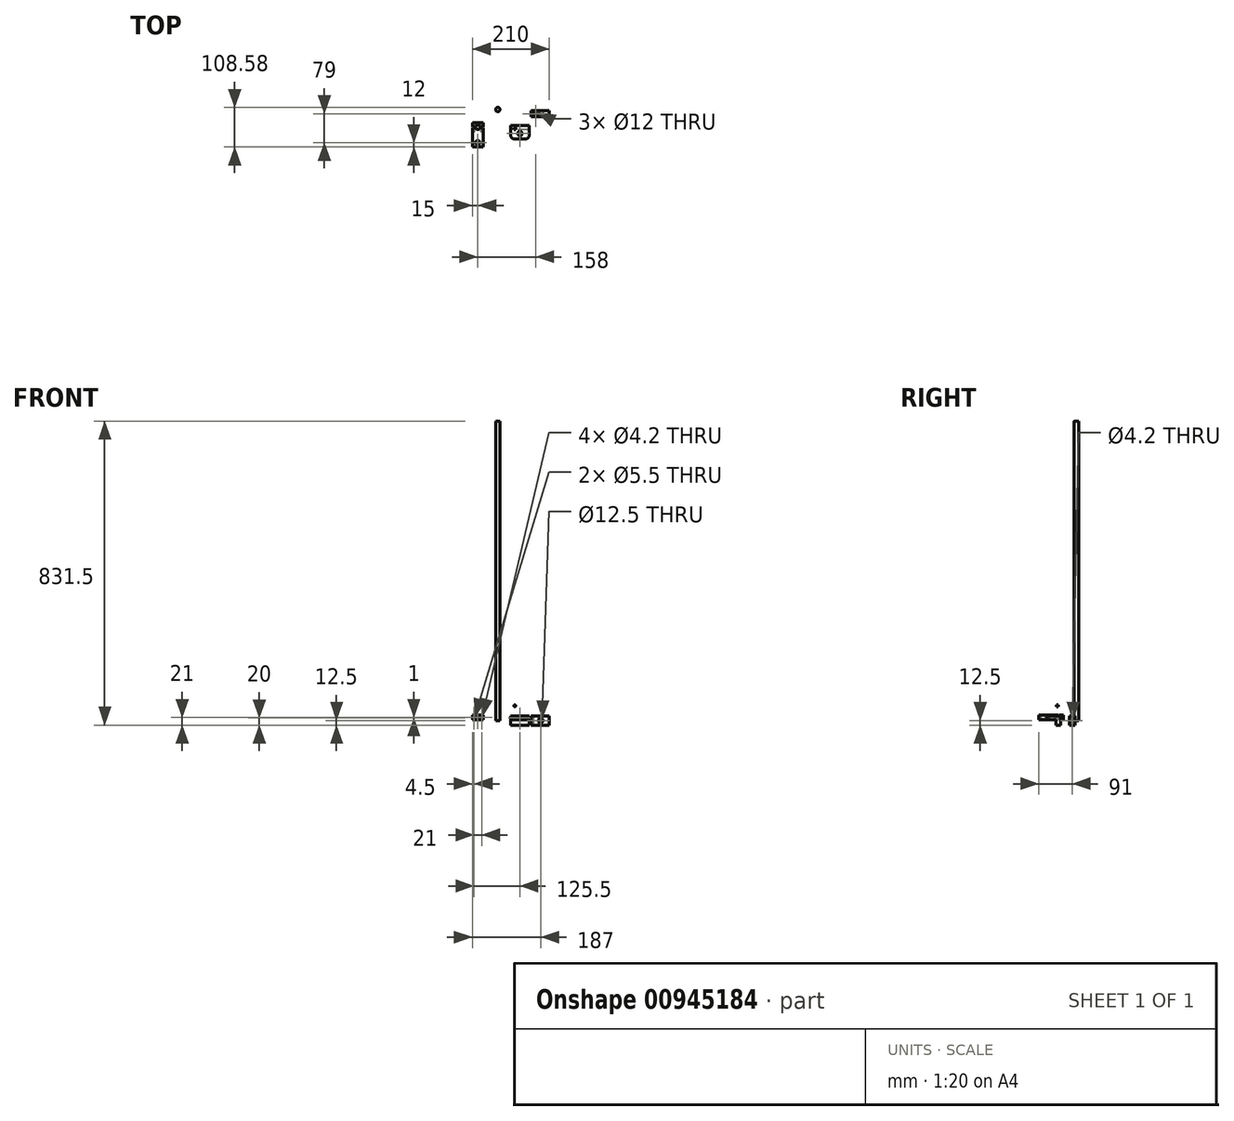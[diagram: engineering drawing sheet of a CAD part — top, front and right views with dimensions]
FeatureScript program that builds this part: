
annotation { "Feature Type Name" : "Feature", "Feature Type Description" : "" }
export const myFeature = defineFeature(function(context is Context, id is Id, definition is map)
    precondition{}
    {
        {
            var Q0;
            Q0=qCreatedBy(makeId("Front.planeOp"),FACE);
            var sketch = newSketch(context, id + "F0", { "sketchPlane" : qUnion([Q0])});
            skLineSegment(sketch, "E0.bottom", {"start": v(25, 12.5) * mm, "end": v(-25, 12.5) * mm});
            skLineSegment(sketch, "E0.top", {"start": v(25, -12.5) * mm, "end": v(-25, -12.5) * mm});
            skLineSegment(sketch, "E0.left", {"start": v(25, 12.5) * mm, "end": v(25, -12.5) * mm});
            skLineSegment(sketch, "E0.right", {"start": v(-25, 12.5) * mm, "end": v(-25, -12.5) * mm});
            skPoint(sketch, "E0.middle", {"position": v(0, 0) * mm});
            skSolve(sketch);
        }
        {
            var Q0;
            Q0 = qSketchRegion(id + "F0", true);
            extrude(context, id + "F1", {"entities" : qUnion([Q0]), "endBound" : BoundingType.SYMMETRIC, "depth" : 12 * mm, "offsetDistance" : 25 * mm});
        }
        {
            var Q0;
            Q0=makeQuery(id+"F1.opExtrude","CAP_FACE",FACE,{"disambiguationData":[OSD([sQuery(id+"F0.wireOp",EDGE,"E0.bottom"),sQuery(id+"F0.wireOp",EDGE,"E0.top"),sQuery(id+"F0.wireOp",EDGE,"E0.left"),sQuery(id+"F0.wireOp",EDGE,"E0.right")])],"isStart":false});
            var sketch = newSketch(context, id + "F2", { "sketchPlane" : qUnion([Q0])});
            skLineSegment(sketch, "E1.bottom", {"start": v(-25, 12.5) * mm, "end": v(25, 12.5) * mm});
            skLineSegment(sketch, "E1.top", {"start": v(-25, 2.5) * mm, "end": v(25, 2.5) * mm});
            skLineSegment(sketch, "E1.left", {"start": v(-25, 12.5) * mm, "end": v(-25, 2.5) * mm});
            skLineSegment(sketch, "E1.right", {"start": v(25, 12.5) * mm, "end": v(25, 2.5) * mm});
            skSolve(sketch);
        }
        {
            var Q0;
            Q0 = qSketchRegion(id + "F2", true);
            extrude(context, id + "F3", {"entities" : qUnion([Q0]), "operationType" : NewBodyOperationType.ADD, "depth" : 25 * mm, "offsetDistance" : 25 * mm});
        }
        {
            var Q0;
            Q0=makeQuery(id+"F3.boolean.opBoolean","MERGE",FACE,{"derivedFrom":[makeQuery(id+"F1.opExtrude","SWEPT_FACE",FACE,{"disambiguationData":[OSD([sQuery(id+"F0.wireOp",EDGE,"E0.bottom")])]}),makeQuery(id+"F3.opExtrude","SWEPT_FACE",FACE,{"disambiguationData":[OSD([sQuery(id+"F2.wireOp",EDGE,"E1.bottom")])]})]});
            var sketch = newSketch(context, id + "F4", { "sketchPlane" : qUnion([Q0])});
            skCircle(sketch, "E2", {"center": v(0, -16) * mm, "radius": 6 * mm});
            skSolve(sketch);
        }
        {
            var Q0;
            Q0 = qSketchRegion(id + "F4", true);
            extrude(context, id + "F5", {"entities" : qUnion([Q0]), "operationType" : NewBodyOperationType.REMOVE, "endBound" : BoundingType.THROUGH_ALL, "oppositeDirection" : true, "depth" : 25 * mm, "offsetDistance" : 25 * mm});
        }
        {
            var Q0;
            Q0=makeQuery(id+"F3.opExtrude","CAP_EDGE",EDGE,{"disambiguationData":[OSD([sQuery(id+"F2.wireOp",EDGE,"E1.left")])],"isStart":false});
            var Q1;
            Q1=makeQuery(id+"F3.opExtrude","CAP_EDGE",EDGE,{"disambiguationData":[OSD([sQuery(id+"F2.wireOp",EDGE,"E1.right")])],"isStart":false});
            fillet(context, id + "F6", {"entities" : qUnion([Q0, Q1]), "radius" : 10 * mm, "tangentPropagation" : true, "allowEdgeOverflow" : false});
        }
        {
            var Q0;
            Q0=qCreatedBy(makeId("Front.planeOp"),FACE);
            var sketch = newSketch(context, id + "F7", { "sketchPlane" : qUnion([Q0])});
            skLineSegment(sketch, "E3.bottom", {"start": v(-130, 14.5) * mm, "end": v(-100, 14.5) * mm});
            skLineSegment(sketch, "E3.top", {"start": v(-130, 2.5) * mm, "end": v(-100, 2.5) * mm});
            skLineSegment(sketch, "E3.left", {"start": v(-130, 14.5) * mm, "end": v(-130, 2.5) * mm});
            skLineSegment(sketch, "E3.right", {"start": v(-100, 14.5) * mm, "end": v(-100, 2.5) * mm});
            skSolve(sketch);
        }
        {
            var Q0;
            Q0 = qSketchRegion(id + "F7", true);
            extrude(context, id + "F8", {"entities" : qUnion([Q0]), "depth" : 53 * mm, "offsetDistance" : 25 * mm});
        }
        {
            var Q0;
            Q0=makeQuery(id+"F8.opExtrude","SWEPT_FACE",FACE,{"disambiguationData":[OSD([sQuery(id+"F7.wireOp",EDGE,"E3.bottom")])]});
            var sketch = newSketch(context, id + "F9", { "sketchPlane" : qUnion([Q0])});
            skCircle(sketch, "E4", {"center": v(-115, 1) * mm, "radius": 6 * mm});
            skSolve(sketch);
        }
        {
            var Q0;
            Q0 = qSketchRegion(id + "F9", true);
            extrude(context, id + "F10", {"entities" : qUnion([Q0]), "operationType" : NewBodyOperationType.REMOVE, "oppositeDirection" : true, "depth" : 25 * mm, "offsetDistance" : 25 * mm});
        }
        {
            var Q0;
            Q0=makeQuery(id+"F8.opExtrude","SWEPT_FACE",FACE,{"disambiguationData":[OSD([sQuery(id+"F7.wireOp",EDGE,"E3.bottom")])]});
            var sketch = newSketch(context, id + "F11", { "sketchPlane" : qUnion([Q0])});
            skLineSegment(sketch, "E5.bottom", {"start": v(-130, 2) * mm, "end": v(-100, 2) * mm});
            skLineSegment(sketch, "E5.top", {"start": v(-130, 14) * mm, "end": v(-100, 14) * mm});
            skLineSegment(sketch, "E5.left", {"start": v(-130, 2) * mm, "end": v(-130, 14) * mm});
            skLineSegment(sketch, "E5.right", {"start": v(-100, 2) * mm, "end": v(-100, 14) * mm});
            skSolve(sketch);
        }
        {
            var Q0;
            Q0 = qSketchRegion(id + "F11", true);
            extrude(context, id + "F12", {"entities" : qUnion([Q0]), "oppositeDirection" : true, "depth" : 12 * mm, "offsetDistance" : 25 * mm});
        }
        {
            var Q0;
            Q0=makeQuery(id+"F12.opExtrude","CAP_FACE",FACE,{"disambiguationData":[OSD([sQuery(id+"F11.wireOp",EDGE,"E5.bottom"),sQuery(id+"F11.wireOp",EDGE,"E5.top"),sQuery(id+"F11.wireOp",EDGE,"E5.left"),sQuery(id+"F11.wireOp",EDGE,"E5.right")])],"isStart":true});
            var sketch = newSketch(context, id + "F13", { "sketchPlane" : qUnion([Q0])});
            skCircle(sketch, "E6", {"center": v(-115, 1) * mm, "radius": 6 * mm});
            skPoint(sketch, "E6.centerSnap0", {"position": v(-115, 2) * mm});
            skSolve(sketch);
        }
        {
            var Q0;
            Q0 = qSketchRegion(id + "F13", true);
            extrude(context, id + "F14", {"entities" : qUnion([Q0]), "operationType" : NewBodyOperationType.REMOVE, "endBound" : BoundingType.THROUGH_ALL, "oppositeDirection" : true, "depth" : 25 * mm, "offsetDistance" : 25 * mm});
        }
        {
            var Q0;
            Q0=makeQuery(id+"F8.opExtrude","SWEPT_FACE",FACE,{"disambiguationData":[OSD([sQuery(id+"F7.wireOp",EDGE,"E3.bottom")])]});
            var sketch = newSketch(context, id + "F15", { "sketchPlane" : qUnion([Q0])});
            skCircle(sketch, "E7", {"center": v(-115, -41) * mm, "radius": 6 * mm});
            skSolve(sketch);
        }
        {
            var Q0;
            Q0 = qSketchRegion(id + "F15", true);
            extrude(context, id + "F16", {"entities" : qUnion([Q0]), "operationType" : NewBodyOperationType.REMOVE, "endBound" : BoundingType.THROUGH_ALL, "oppositeDirection" : true, "depth" : 25 * mm, "offsetDistance" : 25 * mm});
        }
        {
            var Q0;
            Q0=qCreatedBy(makeId("Top.planeOp"),FACE);
            var sketch = newSketch(context, id + "F17", { "sketchPlane" : qUnion([Q0])});
            skCircle(sketch, "E8", {"center": v(-60.48, 49.58) * mm, "radius": 6 * mm});
            skSolve(sketch);
        }
        {
            var Q0;
            Q0 = qSketchRegion(id + "F17", true);
            extrude(context, id + "F18", {"entities" : qUnion([Q0]), "depth" : 819 * mm, "offsetDistance" : 25 * mm});
        }
        {
            var Q0;
            Q0=qCreatedBy(makeId("Top.planeOp"),FACE);
            var sketch = newSketch(context, id + "F19", { "sketchPlane" : qUnion([Q0])});
            skCircle(sketch, "E9", {"center": v(43, 38) * mm, "radius": 6 * mm});
            skLineSegment(sketch, "E10.bottom", {"start": v(30, 30) * mm, "end": v(80, 30) * mm});
            skLineSegment(sketch, "E10.top", {"start": v(30, 46) * mm, "end": v(80, 46) * mm});
            skLineSegment(sketch, "E10.left", {"start": v(30, 30) * mm, "end": v(30, 46) * mm});
            skLineSegment(sketch, "E10.right", {"start": v(80, 30) * mm, "end": v(80, 46) * mm});
            skSolve(sketch);
        }
        {
            var Q0;
            Q0 = qSketchRegion(id + "F19", true);
            extrude(context, id + "F20", {"entities" : qUnion([Q0]), "endBound" : BoundingType.SYMMETRIC, "depth" : 25 * mm, "offsetDistance" : 25 * mm});
        }
        {
            var Q0;
            Q0=makeQuery(id+"F20.opExtrude","SWEPT_FACE",FACE,{"disambiguationData":[OSD([sQuery(id+"F19.wireOp",EDGE,"E10.bottom")])]});
            var sketch = newSketch(context, id + "F21", { "sketchPlane" : qUnion([Q0])});
            skCircle(sketch, "E11", {"center": v(57, 0) * mm, "radius": 6.25 * mm});
            skSolve(sketch);
        }
        {
            var Q0;
            Q0 = qSketchRegion(id + "F21", true);
            extrude(context, id + "F22", {"entities" : qUnion([Q0]), "operationType" : NewBodyOperationType.REMOVE, "oppositeDirection" : true, "depth" : 25 * mm, "offsetDistance" : 25 * mm});
        }
        {
            var Q0;
            Q0=makeQuery(id+"F3.opExtrude","CAP_FACE",FACE,{"disambiguationData":[OSD([sQuery(id+"F2.wireOp",EDGE,"E1.bottom"),sQuery(id+"F2.wireOp",EDGE,"E1.top"),sQuery(id+"F2.wireOp",EDGE,"E1.left"),sQuery(id+"F2.wireOp",EDGE,"E1.right")])],"isStart":false});
            var sketch = newSketch(context, id + "F23", { "sketchPlane" : qUnion([Q0])});
            skPoint(sketch, "E12", {"position": v(0, 7.5) * mm});
            skSolve(sketch);
        }
        {
            var Q0;
            Q0=sQuery(id+"F23.wireOp",VERTEX,"E12");
            var Q1;
            Q1=makeQuery(id+"F1.opExtrude","SWEPT_BODY",BODY,{"disambiguationData":[OSD([sQuery(id+"F0.wireOp",EDGE,"E0.bottom"),sQuery(id+"F0.wireOp",EDGE,"E0.top"),sQuery(id+"F0.wireOp",EDGE,"E0.left"),sQuery(id+"F0.wireOp",EDGE,"E0.right")])]});
            hole(context, id + "F24", {"style" : HoleStyle.SIMPLE, "endStyle" : HoleEndStyle.BLIND, "standardTappedOrClearance" : lookupTablePath({ "standard" : "ISO", "engagement" : "75%", "pitch" : "0.8 mm", "size" : "M5", "type" : "Tapped" }), "standardBlindInLast" : lookupTablePath({ "standard" : "ISO", "fit" : "Normal", "engagement" : "75%", "pitch" : "0.8 mm", "size" : "M5", "type" : "Clearance & tapped" }), "holeDiameter" : 4.2 * mm, "majorDiameter" : 5 * mm, "showTappedDepth" : true, "holeDepth" : 10 * mm, "tappedDepth" : 7.6 * mm, "tapClearance" : 3, "startFromSketch" : true, "locations" : qUnion([Q0]), "scope" : qUnion([Q1])});
        }
        {
            var Q0;
            Q0=makeQuery(id+"F12.opExtrude","SWEPT_FACE",FACE,{"disambiguationData":[OSD([sQuery(id+"F11.wireOp",EDGE,"E5.top")])]});
            var sketch = newSketch(context, id + "F25", { "sketchPlane" : qUnion([Q0])});
            skPoint(sketch, "E13", {"position": v(104.5, 8.5) * mm});
            skPoint(sketch, "E13.positionSnap0", {"position": v(100, 8.5) * mm});
            skPoint(sketch, "E14", {"position": v(125.5, 8.5) * mm});
            skPoint(sketch, "E14.positionSnap0", {"position": v(130, 8.5) * mm});
            skSolve(sketch);
        }
        {
            var Q0;
            Q0=sQuery(id+"F25.wireOp",VERTEX,"E13");
            var Q1;
            Q1=sQuery(id+"F25.wireOp",VERTEX,"E14");
            var Q2;
            Q2=makeQuery(id+"F8.opExtrude","SWEPT_BODY",BODY,{"disambiguationData":[OSD([sQuery(id+"F7.wireOp",EDGE,"E3.bottom"),sQuery(id+"F7.wireOp",EDGE,"E3.top"),sQuery(id+"F7.wireOp",EDGE,"E3.left"),sQuery(id+"F7.wireOp",EDGE,"E3.right")])]});
            var Q3;
            Q3=makeQuery(id+"F12.opExtrude","SWEPT_BODY",BODY,{"disambiguationData":[OSD([sQuery(id+"F11.wireOp",EDGE,"E5.bottom"),sQuery(id+"F11.wireOp",EDGE,"E5.top"),sQuery(id+"F11.wireOp",EDGE,"E5.left"),sQuery(id+"F11.wireOp",EDGE,"E5.right")])]});
            hole(context, id + "F26", {"style" : HoleStyle.SIMPLE, "endStyle" : HoleEndStyle.BLIND, "standardTappedOrClearance" : lookupTablePath({ "fit" : "Normal", "standard" : "ISO", "size" : "M5", "type" : "Clearance" }), "standardBlindInLast" : lookupTablePath({ "fit" : "Normal", "standard" : "ISO", "engagement" : "75%", "pitch" : "0.8 mm", "size" : "M5", "type" : "Clearance & tapped" }), "holeDiameter" : 5.5 * mm, "majorDiameter" : 5 * mm, "holeDepth" : 12 * mm, "tappedDepth" : 7.6 * mm, "tapClearance" : 3, "startFromSketch" : true, "locations" : qUnion([Q0, Q1]), "scope" : qUnion([Q2, Q3])});
        }
        {
            var Q0;
            {var subQ0=sQuery(id+"F7.wireOp",EDGE,"E3.bottom");var subQ1=sQuery(id+"F7.wireOp",EDGE,"E3.top");var subQ2=sQuery(id+"F7.wireOp",EDGE,"E3.left");Q0=makeQuery(id+"F10.boolean.opBoolean","SPLIT",FACE,{"disambiguationData":[TD([makeQuery(id+"F8.opExtrude","SWEPT_FACE",FACE,{"disambiguationData":[OSD([subQ2])]})])],"derivedFrom":makeQuery(id+"F8.opExtrude","CAP_FACE",FACE,{"disambiguationData":[OSD([subQ0,subQ1,subQ2,sQuery(id+"F7.wireOp",EDGE,"E3.right")])],"isStart":true})});}
            var sketch = newSketch(context, id + "F27", { "sketchPlane" : qUnion([Q0])});
            skPoint(sketch, "E15", {"position": v(104.5, 8.5) * mm});
            skPoint(sketch, "E16", {"position": v(125.5, 8.5) * mm});
            skPoint(sketch, "E16.positionSnap0", {"position": v(130, 8.5) * mm});
            skSolve(sketch);
        }
        {
            var Q0;
            Q0=sQuery(id+"F27.wireOp",VERTEX,"E15");
            var Q1;
            Q1=sQuery(id+"F27.wireOp",VERTEX,"E16");
            var Q2;
            Q2=makeQuery(id+"F8.opExtrude","SWEPT_BODY",BODY,{"disambiguationData":[OSD([sQuery(id+"F7.wireOp",EDGE,"E3.bottom"),sQuery(id+"F7.wireOp",EDGE,"E3.top"),sQuery(id+"F7.wireOp",EDGE,"E3.left"),sQuery(id+"F7.wireOp",EDGE,"E3.right")])]});
            hole(context, id + "F28", {"style" : HoleStyle.SIMPLE, "endStyle" : HoleEndStyle.BLIND, "standardTappedOrClearance" : lookupTablePath({ "standard" : "ISO", "engagement" : "75%", "pitch" : "0.8 mm", "size" : "M5", "type" : "Tapped" }), "standardBlindInLast" : lookupTablePath({ "standard" : "ISO", "fit" : "Normal", "engagement" : "75%", "pitch" : "0.8 mm", "size" : "M5", "type" : "Clearance & tapped" }), "holeDiameter" : 4.2 * mm, "majorDiameter" : 5 * mm, "showTappedDepth" : true, "holeDepth" : 10 * mm, "tappedDepth" : 7.6 * mm, "tapClearance" : 3, "startFromSketch" : true, "locations" : qUnion([Q0, Q1]), "scope" : qUnion([Q2])});
        }
        {
            var Q0;
            Q0=makeQuery(id+"F8.opExtrude","CAP_FACE",FACE,{"disambiguationData":[OSD([sQuery(id+"F7.wireOp",EDGE,"E3.bottom"),sQuery(id+"F7.wireOp",EDGE,"E3.top"),sQuery(id+"F7.wireOp",EDGE,"E3.left"),sQuery(id+"F7.wireOp",EDGE,"E3.right")])],"isStart":false});
            var sketch = newSketch(context, id + "F29", { "sketchPlane" : qUnion([Q0])});
            skPoint(sketch, "E17", {"position": v(-115, 8.5) * mm});
            skPoint(sketch, "E17.positionSnap0", {"position": v(-130, 8.5) * mm});
            skPoint(sketch, "E17.positionSnap1", {"position": v(-115, 14.5) * mm});
            skSolve(sketch);
        }
        {
            var Q0;
            Q0=sQuery(id+"F29.wireOp",VERTEX,"E17");
            var Q1;
            Q1=makeQuery(id+"F8.opExtrude","SWEPT_BODY",BODY,{"disambiguationData":[OSD([sQuery(id+"F7.wireOp",EDGE,"E3.bottom"),sQuery(id+"F7.wireOp",EDGE,"E3.top"),sQuery(id+"F7.wireOp",EDGE,"E3.left"),sQuery(id+"F7.wireOp",EDGE,"E3.right")])]});
            hole(context, id + "F30", {"style" : HoleStyle.SIMPLE, "endStyle" : HoleEndStyle.BLIND, "standardTappedOrClearance" : lookupTablePath({ "standard" : "ISO", "engagement" : "75%", "pitch" : "0.8 mm", "size" : "M5", "type" : "Tapped" }), "standardBlindInLast" : lookupTablePath({ "standard" : "ISO", "fit" : "Normal", "engagement" : "75%", "pitch" : "0.8 mm", "size" : "M5", "type" : "Clearance & tapped" }), "holeDiameter" : 4.2 * mm, "majorDiameter" : 5 * mm, "showTappedDepth" : true, "holeDepth" : 5 * mm, "tappedDepth" : 2.6 * mm, "tapClearance" : 3, "startFromSketch" : true, "locations" : qUnion([Q0]), "scope" : qUnion([Q1])});
        }
        {
            var Q0;
            Q0=makeQuery(id+"F20.opExtrude","SWEPT_FACE",FACE,{"disambiguationData":[OSD([sQuery(id+"F19.wireOp",EDGE,"E10.left")])]});
            var sketch = newSketch(context, id + "F31", { "sketchPlane" : qUnion([Q0])});
            skPoint(sketch, "E18", {"position": v(-38, 0) * mm});
            skPoint(sketch, "E18.positionSnap0", {"position": v(-46, 0) * mm});
            skPoint(sketch, "E18.positionSnap1", {"position": v(-38, 12.5) * mm});
            skSolve(sketch);
        }
        {
            var Q0;
            Q0=sQuery(id+"F31.wireOp",VERTEX,"E18");
            var Q1;
            Q1=makeQuery(id+"F20.opExtrude","SWEPT_BODY",BODY,{"disambiguationData":[OSD([sQuery(id+"F19.wireOp",EDGE,"E9"),sQuery(id+"F19.wireOp",EDGE,"E10.bottom"),sQuery(id+"F19.wireOp",EDGE,"E10.top"),sQuery(id+"F19.wireOp",EDGE,"E10.left"),sQuery(id+"F19.wireOp",EDGE,"E10.right")])]});
            hole(context, id + "F32", {"style" : HoleStyle.SIMPLE, "endStyle" : HoleEndStyle.BLIND, "standardTappedOrClearance" : lookupTablePath({ "standard" : "ISO", "engagement" : "75%", "pitch" : "0.8 mm", "size" : "M5", "type" : "Tapped" }), "standardBlindInLast" : lookupTablePath({ "standard" : "ISO", "fit" : "Normal", "engagement" : "75%", "pitch" : "0.8 mm", "size" : "M5", "type" : "Clearance & tapped" }), "holeDiameter" : 4.2 * mm, "majorDiameter" : 5 * mm, "showTappedDepth" : true, "holeDepth" : 5 * mm, "tappedDepth" : 2.6 * mm, "tapClearance" : 3, "startFromSketch" : true, "locations" : qUnion([Q0]), "scope" : qUnion([Q1])});
        }
        {
            var Q0;
            Q0=qCreatedBy(makeId("Front.planeOp"),FACE);
            var sketch = newSketch(context, id + "F33", { "sketchPlane" : qUnion([Q0])});
            skCircle(sketch, "E19", {"center": v(-13.86, 40.11) * mm, "radius": 2.5 * mm});
            skSolve(sketch);
        }
        {
            var Q0;
            Q0 = qSketchRegion(id + "F33", true);
            extrude(context, id + "F34", {"entities" : qUnion([Q0]), "depth" : 5 * mm, "offsetDistance" : 25 * mm});
        }
    });
